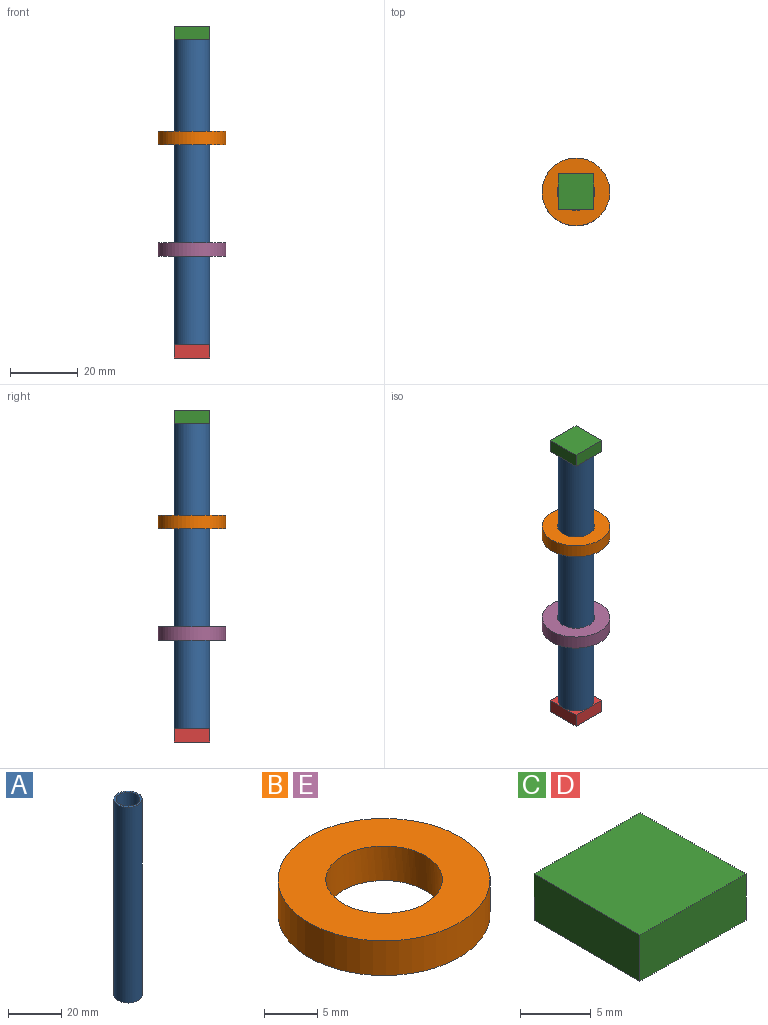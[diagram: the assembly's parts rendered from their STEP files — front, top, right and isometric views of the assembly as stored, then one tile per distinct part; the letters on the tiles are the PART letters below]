
ASSEMBLY  parts=5 mates=4
PART A: 4 faces, bbox 10.6x10.6x90 mm
  f0: cylinder r=5.3mm len=90mm, axis (0,0,1), area 2997.1mm2, adj f1,f2
  f1: plane 10.6x10.6mm, normal (0,0,-1), area 24.6mm2, adj f0,f3
  f2: plane 10.6x10.6mm, normal (0,0,1), area 24.6mm2, adj f0,f3
  f3: cylinder r=4.5mm len=90mm, axis (0,0,1), area 2544.7mm2, adj f1,f2
PART B: 4 faces, bbox 20x20x4 mm
  f0: cylinder r=10mm len=20mm, axis (0,0,-1), area 251.3mm2, adj f1,f2
  f1: plane 20x20mm, normal (0,0,1), area 219.1mm2, adj f0,f3
  f2: plane 20x20mm, normal (0,0,-1), area 219.1mm2, adj f0,f3
  f3: cylinder r=5.5mm len=11mm, axis (0,0,-1), area 138.2mm2, adj f1,f2
PART C: 6 faces, bbox 10.6x10.6x4 mm
  f0: plane 10.6x4mm, normal (0,1,0), area 42.4mm2, adj f1,f3,f4,f5
  f1: plane 10.6x4mm, normal (-1,0,0), area 42.4mm2, adj f0,f2,f4,f5
  f2: plane 10.6x4mm, normal (0,-1,0), area 42.4mm2, adj f1,f3,f4,f5
  f3: plane 10.6x4mm, normal (1,0,0), area 42.4mm2, adj f0,f2,f4,f5
  f4: plane 10.6x10.6mm, normal (0,0,1), area 112.4mm2, adj f0,f1,f2,f3
  f5: plane 10.6x10.6mm, normal (0,0,-1), area 112.4mm2, adj f0,f1,f2,f3
PART D: same geometry as C
PART E: same geometry as B
PLACE A t=(-6.87,-22.98,16.48)mm
PLACE B t=(-6.87,-22.98,-14.52)mm
PLACE C t=(-3.68,-21.78,16.48)mm
PLACE D t=(-3.68,-21.78,-77.52)mm
PLACE E t=(-6.87,-22.98,-47.52)mm
MATE cylindrical B.f3 <-> A.f0  axis (0,0,-1) through (-6.87,-22.98,-10.52)mm
MATE cylindrical E.f3 <-> A.f0  axis (0,0,-1) through (-6.87,-22.98,-47.52)mm
MATE fastened C.f5 <-> A.f0  axis (0,0,-1) through (-6.87,-22.98,16.48)mm
MATE fastened D.f4 <-> A.f0  axis (0,0,1) through (-6.87,-22.98,-73.52)mm
